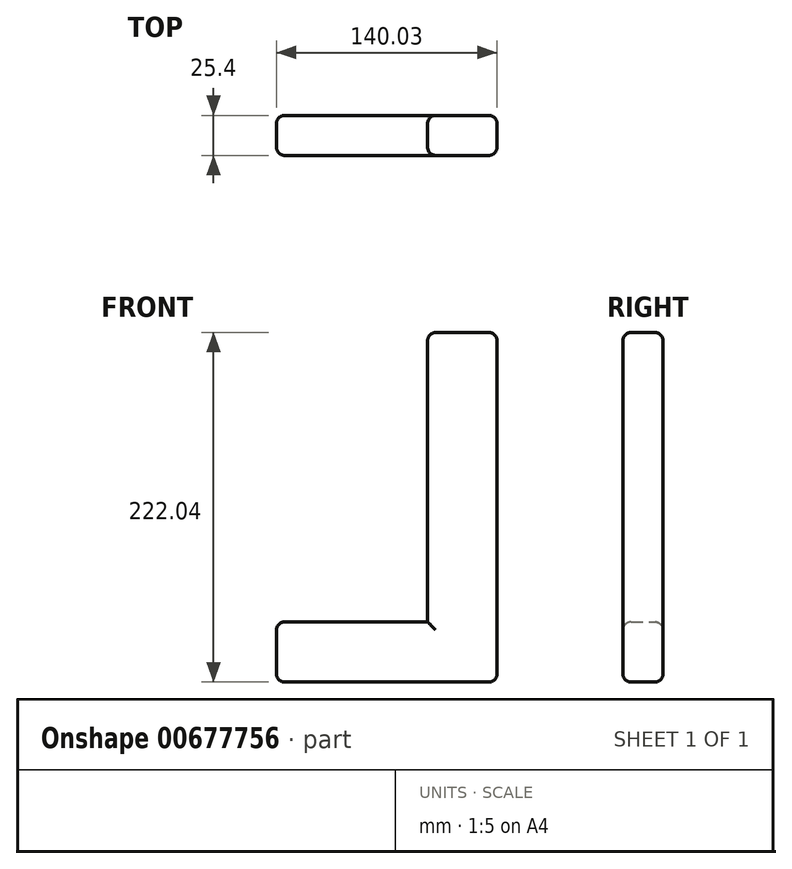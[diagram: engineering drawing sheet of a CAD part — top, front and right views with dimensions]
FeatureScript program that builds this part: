
annotation { "Feature Type Name" : "Feature", "Feature Type Description" : "" }
export const myFeature = defineFeature(function(context is Context, id is Id, definition is map)
    precondition{}
    {
        {
            var Q0;
            Q0=qCreatedBy(makeId("Front.planeOp"),FACE);
            var sketch = newSketch(context, id + "F0", { "sketchPlane" : qUnion([Q0])});
            skLineSegment(sketch, "E0.bottom", {"start": v(0, 103.9) * mm, "end": v(44, 103.9) * mm});
            skLineSegment(sketch, "E0.top", {"start": v(0, -118.13) * mm, "end": v(44, -118.13) * mm});
            skLineSegment(sketch, "E0.left", {"start": v(0, 103.9) * mm, "end": v(0, -79.93) * mm});
            skLineSegment(sketch, "E0.right", {"start": v(44, 103.9) * mm, "end": v(44, -118.13) * mm});
            skLineSegment(sketch, "E1.bottom", {"start": v(-96.03, -118.13) * mm, "end": v(0, -118.13) * mm});
            skLineSegment(sketch, "E1.top", {"start": v(-96.03, -79.93) * mm, "end": v(0, -79.93) * mm});
            skLineSegment(sketch, "E1.left", {"start": v(-96.03, -118.13) * mm, "end": v(-96.03, -79.93) * mm});
            skCircle(sketch, "E2", {"center": v(-79.04, -65.2) * mm, "radius": 7.45 * mm});
            skSolve(sketch);
        }
        {
            var Q0;
            Q0 = qSketchRegion(id + "F0", true);
            var sketch = newSketch(context, id + "F1", { "sketchPlane" : qUnion([Q0])});
            skSolve(sketch);
        }
        {
            var Q0;
            Q0=makeQuery(id+"F1.imprint","IMPRINT",FACE,{"disambiguationData":[TD([[makeQuery(id+"F1.imprint","IMPRINT",EDGE,{"derivedFrom":makeQuery(id+"F0.imprint","IMPRINT",EDGE,{"derivedFrom":sQuery(id+"F0.wireOp",EDGE,"E0.bottom")})}),-1.0]])]});
            extrude(context, id + "F2", {"entities" : qUnion([Q0]), "depth" : 25.4 * mm, "offsetDistance" : 25.4 * mm});
        }
        {
            var Q0;
            Q0=makeQuery(id+"F2.opExtrude","CAP_FACE",FACE,{"disambiguationData":[OSD([sQuery(id+"F0.wireOp",EDGE,"E0.bottom"),sQuery(id+"F0.wireOp",EDGE,"E0.top"),sQuery(id+"F0.wireOp",EDGE,"E0.left"),sQuery(id+"F0.wireOp",EDGE,"E0.right"),sQuery(id+"F0.wireOp",EDGE,"E1.bottom"),sQuery(id+"F0.wireOp",EDGE,"E1.top"),sQuery(id+"F0.wireOp",EDGE,"E1.left")])],"isStart":false});
            fillet(context, id + "F3", {"entities" : qUnion([Q0]), "radius" : 5.08 * mm, "tangentPropagation" : true, "allowEdgeOverflow" : false});
        }
        {
            var Q0;
            {var subQ0=sQuery(id+"F0.wireOp",EDGE,"E1.bottom");var subQ1=sQuery(id+"F0.wireOp",EDGE,"E0.top");Q0=makeQuery(id+"F3.opFillet","BLEND_EDGE",EDGE,{"blendedFrom":[makeQuery(id+"F2.opExtrude","CAP_EDGE",EDGE,{"disambiguationData":[OSD([subQ1,subQ0])],"isStart":false}),makeQuery(id+"F2.opExtrude","SWEPT_FACE",FACE,{"disambiguationData":[OSD([subQ1,subQ0])]})],"blendedInto":[makeQuery(id+"F2.opExtrude","SWEPT_FACE",FACE,{"disambiguationData":[OSD([subQ1,subQ0])]})]});}
            var Q1;
            Q1=makeQuery(id+"F2.opExtrude","SWEPT_EDGE",EDGE,{"disambiguationData":[OSD([sQuery(id+"F0.wireOp",EDGE,"E1.bottom"),sQuery(id+"F0.wireOp",EDGE,"E1.left")])]});
            fillet(context, id + "F4", {"entities" : qUnion([Q0, Q1]), "radius" : 5.08 * mm, "tangentPropagation" : true, "allowEdgeOverflow" : false});
        }
        {
            var Q0;
            Q0=makeQuery(id+"F2.opExtrude","CAP_FACE",FACE,{"disambiguationData":[OSD([sQuery(id+"F0.wireOp",EDGE,"E0.bottom"),sQuery(id+"F0.wireOp",EDGE,"E0.top"),sQuery(id+"F0.wireOp",EDGE,"E0.left"),sQuery(id+"F0.wireOp",EDGE,"E0.right"),sQuery(id+"F0.wireOp",EDGE,"E1.bottom"),sQuery(id+"F0.wireOp",EDGE,"E1.top"),sQuery(id+"F0.wireOp",EDGE,"E1.left")])],"isStart":true});
            fillet(context, id + "F5", {"entities" : qUnion([Q0]), "radius" : 5.08 * mm, "tangentPropagation" : true, "allowEdgeOverflow" : false});
        }
        {
            var Q0;
            Q0=makeQuery(id+"F2.opExtrude","SWEPT_EDGE",EDGE,{"disambiguationData":[OSD([sQuery(id+"F0.wireOp",EDGE,"E1.top"),sQuery(id+"F0.wireOp",EDGE,"E1.left")])]});
            var Q1;
            Q1=makeQuery(id+"F2.opExtrude","SWEPT_EDGE",EDGE,{"disambiguationData":[OSD([sQuery(id+"F0.wireOp",EDGE,"E0.bottom"),sQuery(id+"F0.wireOp",EDGE,"E0.left")])]});
            var Q2;
            Q2=makeQuery(id+"F2.opExtrude","SWEPT_EDGE",EDGE,{"disambiguationData":[OSD([sQuery(id+"F0.wireOp",EDGE,"E0.bottom"),sQuery(id+"F0.wireOp",EDGE,"E0.right")])]});
            fillet(context, id + "F6", {"entities" : qUnion([Q0, Q1, Q2]), "radius" : 5.08 * mm, "tangentPropagation" : true, "allowEdgeOverflow" : false});
        }
        {
            var Q0;
            Q0=makeQuery(id+"F2.opExtrude","SWEPT_EDGE",EDGE,{"disambiguationData":[OSD([sQuery(id+"F0.wireOp",EDGE,"E0.top"),sQuery(id+"F0.wireOp",EDGE,"E0.right")])]});
            fillet(context, id + "F7", {"entities" : qUnion([Q0]), "radius" : 5.08 * mm, "tangentPropagation" : true, "allowEdgeOverflow" : false});
        }
    });
